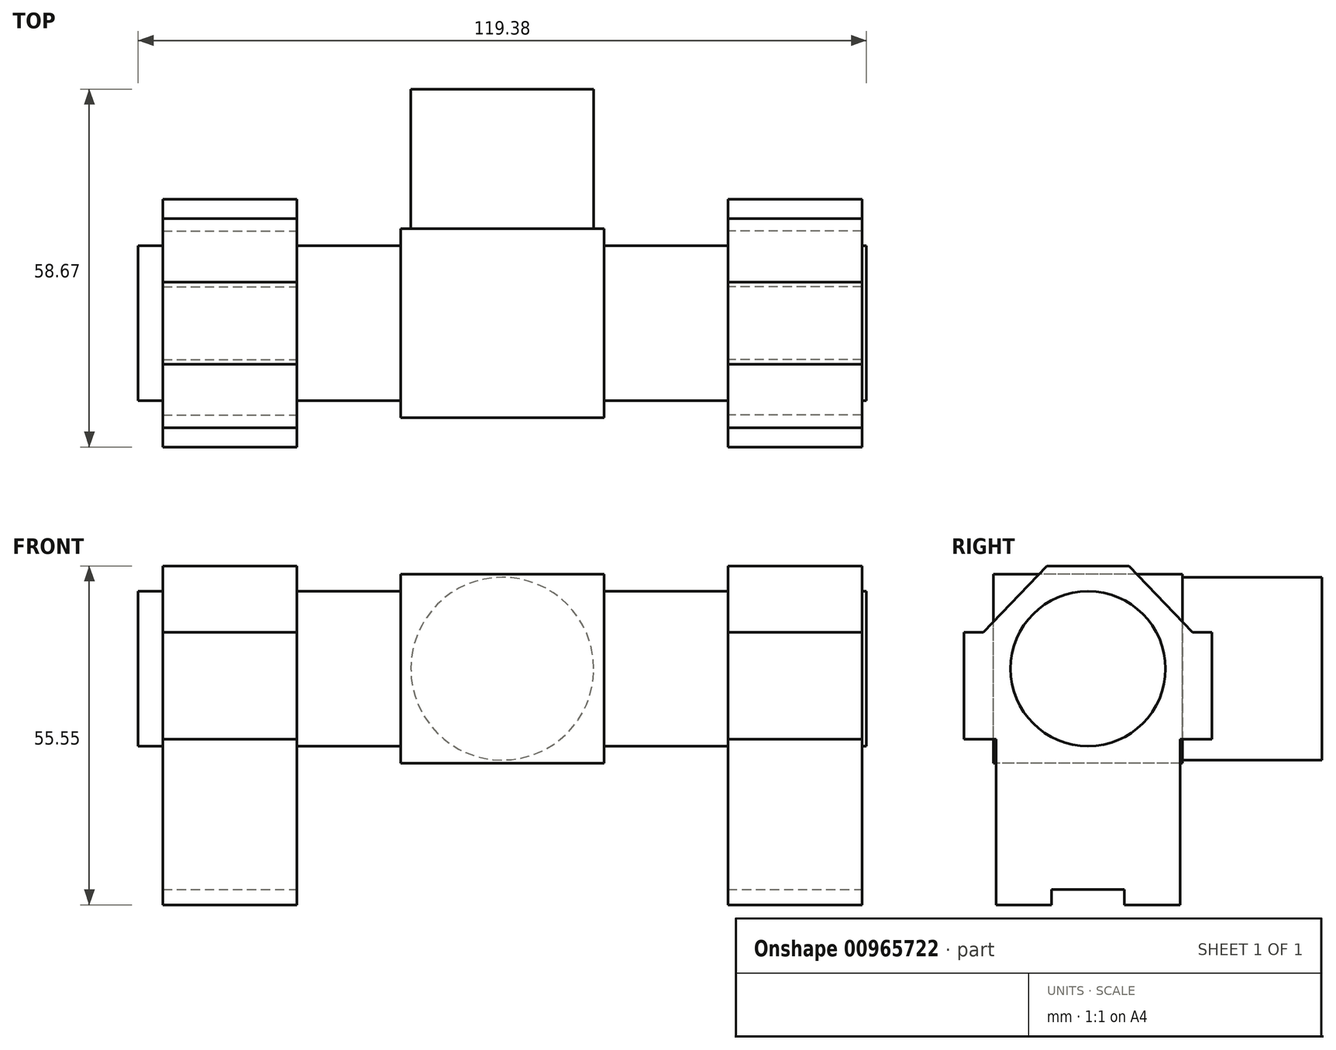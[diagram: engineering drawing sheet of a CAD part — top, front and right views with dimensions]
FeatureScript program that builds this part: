
annotation { "Feature Type Name" : "Feature", "Feature Type Description" : "" }
export const myFeature = defineFeature(function(context is Context, id is Id, definition is map)
    precondition{}
    {
        {
            var Q0;
            Q0=qCreatedBy(makeId("Right.planeOp"),FACE);
            var sketch = newSketch(context, id + "F0", { "sketchPlane" : qUnion([Q0])});
            skCircle(sketch, "E0", {"center": v(0, 0) * mm, "radius": 12.7 * mm});
            skSolve(sketch);
        }
        {
            var Q0;
            Q0=makeQuery(id+"F0.imprint","IMPRINT",FACE,{"disambiguationData":[TD([[makeQuery(id+"F0.imprint","IMPRINT",EDGE,{"derivedFrom":sQuery(id+"F0.wireOp",EDGE,"E0")}),1.0]])]});
            extrude(context, id + "F1", {"entities" : qUnion([Q0]), "endBound" : BoundingType.SYMMETRIC, "depth" : 119.38 * mm, "offsetDistance" : 25.4 * mm});
        }
        {
            var Q0;
            Q0=qCreatedBy(makeId("Right.planeOp"),FACE);
            var sketch = newSketch(context, id + "F2", { "sketchPlane" : qUnion([Q0])});
            skLineSegment(sketch, "E1.bottom", {"start": v(15.5, -15.5) * mm, "end": v(-15.5, -15.5) * mm});
            skLineSegment(sketch, "E1.top", {"start": v(15.5, 15.5) * mm, "end": v(-15.5, 15.5) * mm});
            skLineSegment(sketch, "E1.left", {"start": v(15.5, -15.5) * mm, "end": v(15.5, 15.5) * mm});
            skLineSegment(sketch, "E1.right", {"start": v(-15.5, -15.5) * mm, "end": v(-15.5, 15.5) * mm});
            skPoint(sketch, "E1.middle", {"position": v(0, 0) * mm});
            skSolve(sketch);
        }
        {
            var Q0;
            Q0=makeQuery(id+"F2.imprint","IMPRINT",FACE,{"disambiguationData":[TD([[makeQuery(id+"F2.imprint","IMPRINT",EDGE,{"derivedFrom":sQuery(id+"F2.wireOp",EDGE,"E1.bottom")}),-1.0]])]});
            extrude(context, id + "F3", {"entities" : qUnion([Q0]), "operationType" : NewBodyOperationType.ADD, "endBound" : BoundingType.SYMMETRIC, "depth" : 33.32 * mm, "offsetDistance" : 25.4 * mm});
        }
        {
            var Q0;
            Q0=makeQuery(id+"F3.opExtrude","CAP_FACE",FACE,{"disambiguationData":[OSD([sQuery(id+"F2.wireOp",EDGE,"E1.bottom"),sQuery(id+"F2.wireOp",EDGE,"E1.top"),sQuery(id+"F2.wireOp",EDGE,"E1.left"),sQuery(id+"F2.wireOp",EDGE,"E1.right")])],"isStart":true});
            cPlane(context, id + "F4", {"entities" : qUnion([Q0]), "cplaneType" : CPlaneType.OFFSET, "offset" : 17.02 * mm, "width" : 152.4 * mm, "height" : 152.4 * mm});
        }
        {
            var Q0;
            Q0=makeQuery(id+"F3.opExtrude","CAP_FACE",FACE,{"disambiguationData":[OSD([sQuery(id+"F2.wireOp",EDGE,"E1.bottom"),sQuery(id+"F2.wireOp",EDGE,"E1.top"),sQuery(id+"F2.wireOp",EDGE,"E1.left"),sQuery(id+"F2.wireOp",EDGE,"E1.right")])],"isStart":false});
            cPlane(context, id + "F5", {"entities" : qUnion([Q0]), "cplaneType" : CPlaneType.OFFSET, "offset" : 20.32 * mm, "width" : 152.4 * mm, "height" : 152.4 * mm});
        }
        {
            var Q0;
            Q0=qCreatedBy(id+"F5.planeOp",FACE);
            var sketch = newSketch(context, id + "F6", { "sketchPlane" : qUnion([Q0])});
            skLineSegment(sketch, "E2", {"start": v(-25.07, 12.7) * mm, "end": v(26.97, 12.7) * mm, "construction": true});
            skLineSegment(sketch, "E3.0", {"start": v(-20.32, -11.56) * mm, "end": v(-15.07, -11.56) * mm});
            skLineSegment(sketch, "E4.0", {"start": v(-20.32, 5.97) * mm, "end": v(-17.15, 5.97) * mm});
            skLineSegment(sketch, "E5", {"start": v(0, -42.06) * mm, "end": v(0, 0) * mm, "construction": true});
            skLineSegment(sketch, "E6.0", {"start": v(-20.32, -11.56) * mm, "end": v(-20.32, 5.97) * mm});
            skLineSegment(sketch, "E7.trimOffspring", {"start": v(-6.73, 16.84) * mm, "end": v(0, 16.84) * mm});
            skLineSegment(sketch, "E8", {"start": v(-17.15, 5.97) * mm, "end": v(-6.73, 16.84) * mm});
            skLineSegment(sketch, "E9.0", {"start": v(-15.07, -38.71) * mm, "end": v(0, -38.71) * mm});
            skLineSegment(sketch, "E10.0", {"start": v(-15.07, -38.71) * mm, "end": v(-15.07, -11.56) * mm});
            skLineSegment(sketch, "E11.MirrorCS", {"start": v(6.73, 16.84) * mm, "end": v(0, 16.84) * mm});
            skLineSegment(sketch, "E12.MirrorCS", {"start": v(17.15, 5.97) * mm, "end": v(6.73, 16.84) * mm});
            skLineSegment(sketch, "E13.MirrorCS", {"start": v(20.32, 5.97) * mm, "end": v(17.15, 5.97) * mm});
            skLineSegment(sketch, "E14.MirrorCS", {"start": v(20.32, -11.56) * mm, "end": v(20.32, 5.97) * mm});
            skLineSegment(sketch, "E15.MirrorCS", {"start": v(20.32, -11.56) * mm, "end": v(15.07, -11.56) * mm});
            skLineSegment(sketch, "E16.MirrorCS", {"start": v(15.07, -38.71) * mm, "end": v(15.07, -11.56) * mm});
            skLineSegment(sketch, "E17.MirrorCS", {"start": v(15.07, -38.71) * mm, "end": v(0, -38.71) * mm});
            skSolve(sketch);
        }
        {
            var Q0;
            Q0 = qSketchRegion(id + "F6", true);
            extrude(context, id + "F7", {"entities" : qUnion([Q0]), "operationType" : NewBodyOperationType.ADD, "depth" : 21.97 * mm, "offsetDistance" : 25.4 * mm});
        }
        {
            var Q0;
            Q0=qCreatedBy(id+"F4.planeOp",FACE);
            var sketch = newSketch(context, id + "F8", { "sketchPlane" : qUnion([Q0])});
            skLineSegment(sketch, "E18.0.0", {"start": v(15.07, -38.71) * mm, "end": v(-15.07, -38.71) * mm});
            skLineSegment(sketch, "E18.0.1", {"start": v(-15.07, -38.71) * mm, "end": v(-15.07, -11.56) * mm});
            skLineSegment(sketch, "E18.0.2", {"start": v(-15.07, -11.56) * mm, "end": v(-20.32, -11.56) * mm});
            skLineSegment(sketch, "E18.0.3", {"start": v(-20.32, -11.56) * mm, "end": v(-20.32, 5.97) * mm});
            skLineSegment(sketch, "E18.0.4", {"start": v(-20.32, 5.97) * mm, "end": v(-17.15, 5.97) * mm});
            skLineSegment(sketch, "E18.0.5", {"start": v(-17.15, 5.97) * mm, "end": v(-6.73, 16.84) * mm});
            skLineSegment(sketch, "E18.0.6", {"start": v(-6.73, 16.84) * mm, "end": v(6.73, 16.84) * mm});
            skLineSegment(sketch, "E18.0.7", {"start": v(6.73, 16.84) * mm, "end": v(17.15, 5.97) * mm});
            skLineSegment(sketch, "E18.0.8", {"start": v(17.15, 5.97) * mm, "end": v(20.32, 5.97) * mm});
            skLineSegment(sketch, "E18.0.9", {"start": v(20.32, 5.97) * mm, "end": v(20.32, -11.56) * mm});
            skLineSegment(sketch, "E18.0.10", {"start": v(20.32, -11.56) * mm, "end": v(15.07, -11.56) * mm});
            skLineSegment(sketch, "E18.0.11", {"start": v(15.07, -11.56) * mm, "end": v(15.07, -38.71) * mm});
            skSolve(sketch);
        }
        {
            var Q0;
            Q0 = qSketchRegion(id + "F8", true);
            extrude(context, id + "F9", {"entities" : qUnion([Q0]), "operationType" : NewBodyOperationType.ADD, "depth" : 21.97 * mm, "offsetDistance" : 25.4 * mm});
        }
        {
            var Q0;
            Q0=makeQuery(id+"F3.opExtrude","SWEPT_FACE",FACE,{"disambiguationData":[OSD([sQuery(id+"F2.wireOp",EDGE,"E1.left")])]});
            var sketch = newSketch(context, id + "F10", { "sketchPlane" : qUnion([Q0])});
            skLineSegment(sketch, "E19", {"start": v(-16.66, 15.5) * mm, "end": v(16.66, -15.5) * mm, "construction": true});
            skLineSegment(sketch, "E20", {"start": v(-16.66, -15.5) * mm, "end": v(0, 0) * mm, "construction": true});
            skCircle(sketch, "E21", {"center": v(0, 0) * mm, "radius": 14.99 * mm});
            skSolve(sketch);
        }
        {
            var Q0;
            Q0=makeQuery(id+"F10.imprint","IMPRINT",FACE,{"disambiguationData":[TD([[makeQuery(id+"F10.imprint","IMPRINT",EDGE,{"derivedFrom":sQuery(id+"F10.wireOp",EDGE,"E21")}),1.0]])]});
            extrude(context, id + "F11", {"entities" : qUnion([Q0]), "operationType" : NewBodyOperationType.ADD, "depth" : 22.86 * mm, "offsetDistance" : 25.4 * mm});
        }
        {
            var Q0;
            Q0=makeQuery(id+"F7.opExtrude","CAP_FACE",FACE,{"disambiguationData":[OSD([sQuery(id+"F6.wireOp",EDGE,"E3.0"),sQuery(id+"F6.wireOp",EDGE,"E4.0"),sQuery(id+"F6.wireOp",EDGE,"E6.0"),sQuery(id+"F6.wireOp",EDGE,"E7.trimOffspring"),sQuery(id+"F6.wireOp",EDGE,"E8"),sQuery(id+"F6.wireOp",EDGE,"E9.0"),sQuery(id+"F6.wireOp",EDGE,"E10.0"),sQuery(id+"F6.wireOp",EDGE,"E11.MirrorCS"),sQuery(id+"F6.wireOp",EDGE,"E12.MirrorCS"),sQuery(id+"F6.wireOp",EDGE,"E13.MirrorCS"),sQuery(id+"F6.wireOp",EDGE,"E14.MirrorCS"),sQuery(id+"F6.wireOp",EDGE,"E15.MirrorCS"),sQuery(id+"F6.wireOp",EDGE,"E16.MirrorCS"),sQuery(id+"F6.wireOp",EDGE,"E17.MirrorCS")])],"isStart":false});
            var sketch = newSketch(context, id + "F12", { "sketchPlane" : qUnion([Q0])});
            skLineSegment(sketch, "E22.bottom", {"start": v(5.97, -41.25) * mm, "end": v(-5.97, -41.25) * mm});
            skLineSegment(sketch, "E22.top", {"start": v(5.97, -36.17) * mm, "end": v(-5.97, -36.17) * mm});
            skLineSegment(sketch, "E22.left", {"start": v(5.97, -41.25) * mm, "end": v(5.97, -36.17) * mm});
            skLineSegment(sketch, "E22.right", {"start": v(-5.97, -41.25) * mm, "end": v(-5.97, -36.17) * mm});
            skPoint(sketch, "E22.middle", {"position": v(0, -38.71) * mm});
            skSolve(sketch);
        }
        {
            var Q0;
            Q0 = qSketchRegion(id + "F12", true);
            extrude(context, id + "F13", {"entities" : qUnion([Q0]), "operationType" : NewBodyOperationType.REMOVE, "endBound" : BoundingType.THROUGH_ALL, "oppositeDirection" : true, "depth" : 25.4 * mm, "offsetDistance" : 25.4 * mm});
        }
    });
